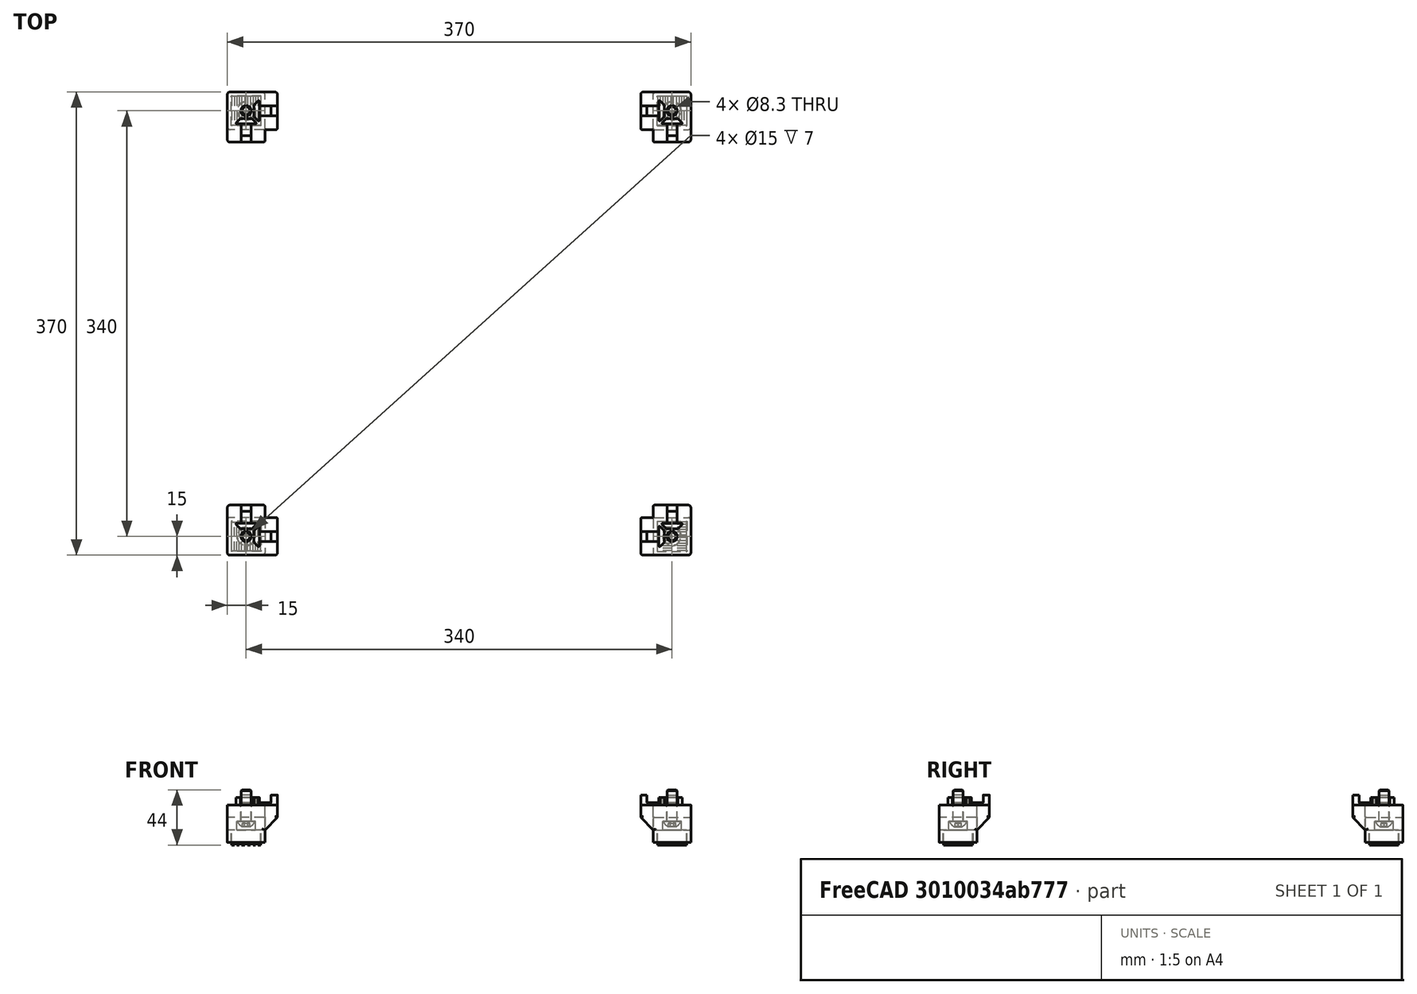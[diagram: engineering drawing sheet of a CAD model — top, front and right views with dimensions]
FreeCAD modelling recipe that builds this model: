
FCSTD DOCUMENT  (FreeCAD 0.19R24291 (Git))
Label: foot-assembly
License: Other
LicenseURL: GPL3
objects: Part::Feature×8, Part::FeaturePython×4, App::Part×1
note: 12 computed .brp shape members not serialized (recipe doc carries the construction recipe); baked Part::Feature solids carry a one-line shape summary decoded from their .brp

FEATURE [Part::Feature] Cut008004003004014002002009  label="rubber-pad003"
  Placement = pos=(170,355,-32) rot=(0,0,1;3.14159rad)
  shape: bbox 23 x 23 x 12 mm, 26 faces (baked)
FEATURE [Part::Feature] Cut008004003004014002002004  label="foot001"
  Placement = pos=(170,15,-30) rot=(0,0,-1;1.5708rad)
  shape: bbox 40.3 x 40.3 x 38.3 mm, 68 faces (baked)
FEATURE [Part::Feature] Cut008004003004014002002010  label="rubber-pad004"
  Placement = pos=(-170,355,-32) rot=(0,0,1;3.14159rad)
  shape: bbox 23 x 23 x 12 mm, 26 faces (baked)
FEATURE [Part::Feature] Cut008004003004014002002006  label="foot003"
  Placement = pos=(-170,355,-30) rot=(0,0,1;1.5708rad)
  shape: bbox 40.3 x 40.3 x 38.3 mm, 68 faces (baked)
FEATURE [Part::Feature] Cut002002001  label="rubber-pad001"
  Placement = pos=(-170,15,-32) rot=(0,0,1;0rad)
  shape: bbox 23 x 23 x 12 mm, 26 faces (baked)
FEATURE [Part::Feature] Cut008004003004014002002007  label="foot004"
  Placement = pos=(170,355,-30) rot=(0,0,1;0rad)
  shape: bbox 40.3 x 40.3 x 38.3 mm, 68 faces (baked)
FEATURE [Part::Feature] Cut008004003004014002002008  label="rubber-pad002"
  Placement = pos=(170,15,-32) rot=(0,0,1;1.5708rad)
  shape: bbox 23 x 23 x 12 mm, 26 faces (baked)
FEATURE [Part::Feature] Cut008004003004014002002005  label="foot002"
  Placement = pos=(-170,15,-30) rot=(0,0,1;3.14159rad)
  shape: bbox 40.3 x 40.3 x 38.3 mm, 68 faces (baked)
FEATURE [Part::FeaturePython] Screw  label="M8x25-Screw"  # Fasteners workbench fastener (typed FeaturePython)
  Placement = pos=(-170,15,-13) rot=(-1,0,0;3.14159rad)
  baseObject = -> Cut008004003004014002002005 [Edge127]
  diameter = 5
  invert = true
  length = 4
  lengthCustom = 25
  matchOuter = true
  offset = 0
  thread = false
  type = 39
FEATURE [Part::FeaturePython] Screw001  label="M8x25-Screw001"  # Fasteners workbench fastener (typed FeaturePython)
  Placement = pos=(-170,355,-13) rot=(-1,0,0;3.14159rad)
  baseObject = -> Cut008004003004014002002006 [Edge127]
  diameter = 5
  invert = true
  length = 4
  lengthCustom = 25
  matchOuter = true
  offset = 0
  thread = false
  type = 39
FEATURE [Part::FeaturePython] Screw002  label="M8x25-Screw002"  # Fasteners workbench fastener (typed FeaturePython)
  Placement = pos=(170,15,-13) rot=(-1,0,0;3.14159rad)
  baseObject = -> Cut008004003004014002002004 [Edge127]
  diameter = 5
  invert = true
  length = 4
  lengthCustom = 25
  matchOuter = true
  offset = 0
  thread = false
  type = 39
FEATURE [Part::FeaturePython] Screw003  label="M8x25-Screw003"  # Fasteners workbench fastener (typed FeaturePython)
  Placement = pos=(170,355,-13) rot=(-1,0,0;3.14159rad)
  baseObject = -> Cut008004003004014002002007 [Edge127]
  diameter = 5
  invert = true
  length = 4
  lengthCustom = 25
  matchOuter = true
  offset = 0
  thread = false
  type = 39
FEATURE [App::Part] Part056  label="foot"
  Group = -> [Cut008004003004014002002004,Cut008004003004014002002005,Cut008004003004014002002006,Cut008004003004014002002007,Cut002002001,Cut008004003004014002002008,Cut008004003004014002002009,Cut008004003004014002002010,Screw,Screw001,Screw002,Screw003]
  Origin = -> Origin058
